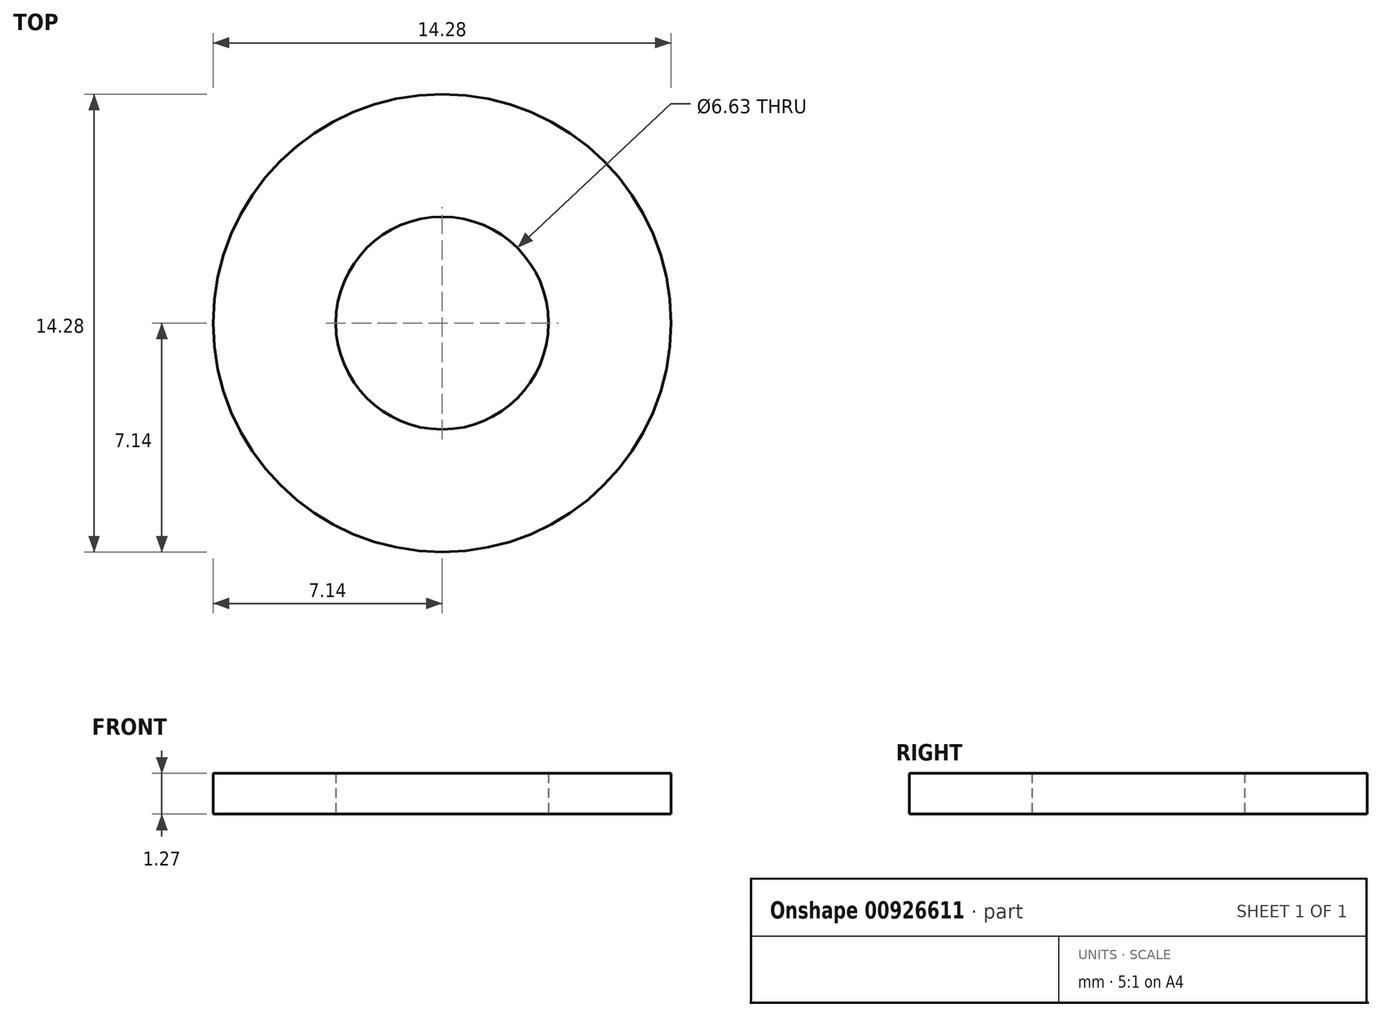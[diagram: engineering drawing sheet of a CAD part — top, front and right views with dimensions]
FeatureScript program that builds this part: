
annotation { "Feature Type Name" : "Feature", "Feature Type Description" : "" }
export const myFeature = defineFeature(function(context is Context, id is Id, definition is map)
    precondition{}
    {
        {
            var Q0;
            Q0=qCreatedBy(makeId("Top.planeOp"),FACE);
            var sketch = newSketch(context, id + "F0", { "sketchPlane" : qUnion([Q0])});
            skCircle(sketch, "E0", {"center": v(0, 0) * mm, "radius": 7.14 * mm});
            skCircle(sketch, "E1", {"center": v(0, 0) * mm, "radius": 3.31 * mm});
            skSolve(sketch);
        }
        {
            var Q0;
            Q0=makeQuery(id+"F0.imprint","IMPRINT",FACE,{"disambiguationData":[TD([[makeQuery(id+"F0.imprint","IMPRINT",EDGE,{"derivedFrom":sQuery(id+"F0.wireOp",EDGE,"E0")}),1.0]])]});
            extrude(context, id + "F1", {"entities" : qUnion([Q0]), "depth" : 1.27 * mm, "offsetDistance" : 25.4 * mm});
        }
    });
